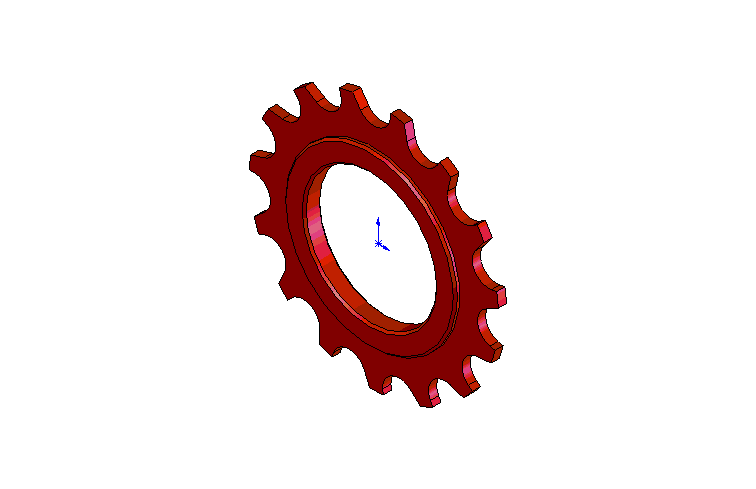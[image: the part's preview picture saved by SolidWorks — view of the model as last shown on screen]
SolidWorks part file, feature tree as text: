
SOLIDWORKS PART (.sldprt)
format: sldprt  version: not decoded by parser v0  size: 324,096 bytes
history: native  units: mm
features: sketch x4, plane x3, extrude x3, material x1, cut_extrude x1, pattern_circular x1, chamfer x1 (+10 scaffold rows collapsed)
feature tree (24):
  scaffold x10  (default folders/planes/origin — collapsed)
  material  "Matériau <non spécifié>"
  plane  "Plan de face"
  plane  "Plan de dessus"
  plane  "Plan de droite"
  sketch  "Esquisse1"  dims[D1=61.0mm]
  extrude  "Extrusion1"  Depth=2mm
  sketch  "Esquisse2"  dims[c1.D1=8.0mm c1.D3=4.0mm c2.D1=8.0mm c2.D3=4.0mm c2.D2=9.5mm c3.D3=4.0mm c3.D2=~2.039916mm c4.D2=35.0deg c4.D3=5.0mm]
  cut_extrude  "Enlèv. mat.-Extru.1"  [1 undecoded]
  pattern_circular  "Répétition circulaire1"  Count=15 Angle=24deg
  sketch  "Esquisse3"  dims[D1=42.0mm]
  extrude  "Extrusion2"  Depth=4.25mm
  sketch  "Esquisse4"  dims[D1=32.0mm]
  extrude  "Enlèv. mat.-Extru.2"  [1 undecoded]
  chamfer  "Chanfrein1"  Distance=0.5mm Angle=45deg
decode coverage: 8 of 10 modeling features carry decoded parameters
note: ~ marks probable driven/reference dimensions
note: 2 parameter values undecoded
note: suppression state not decoded; provenance and decode notes live in map.json
